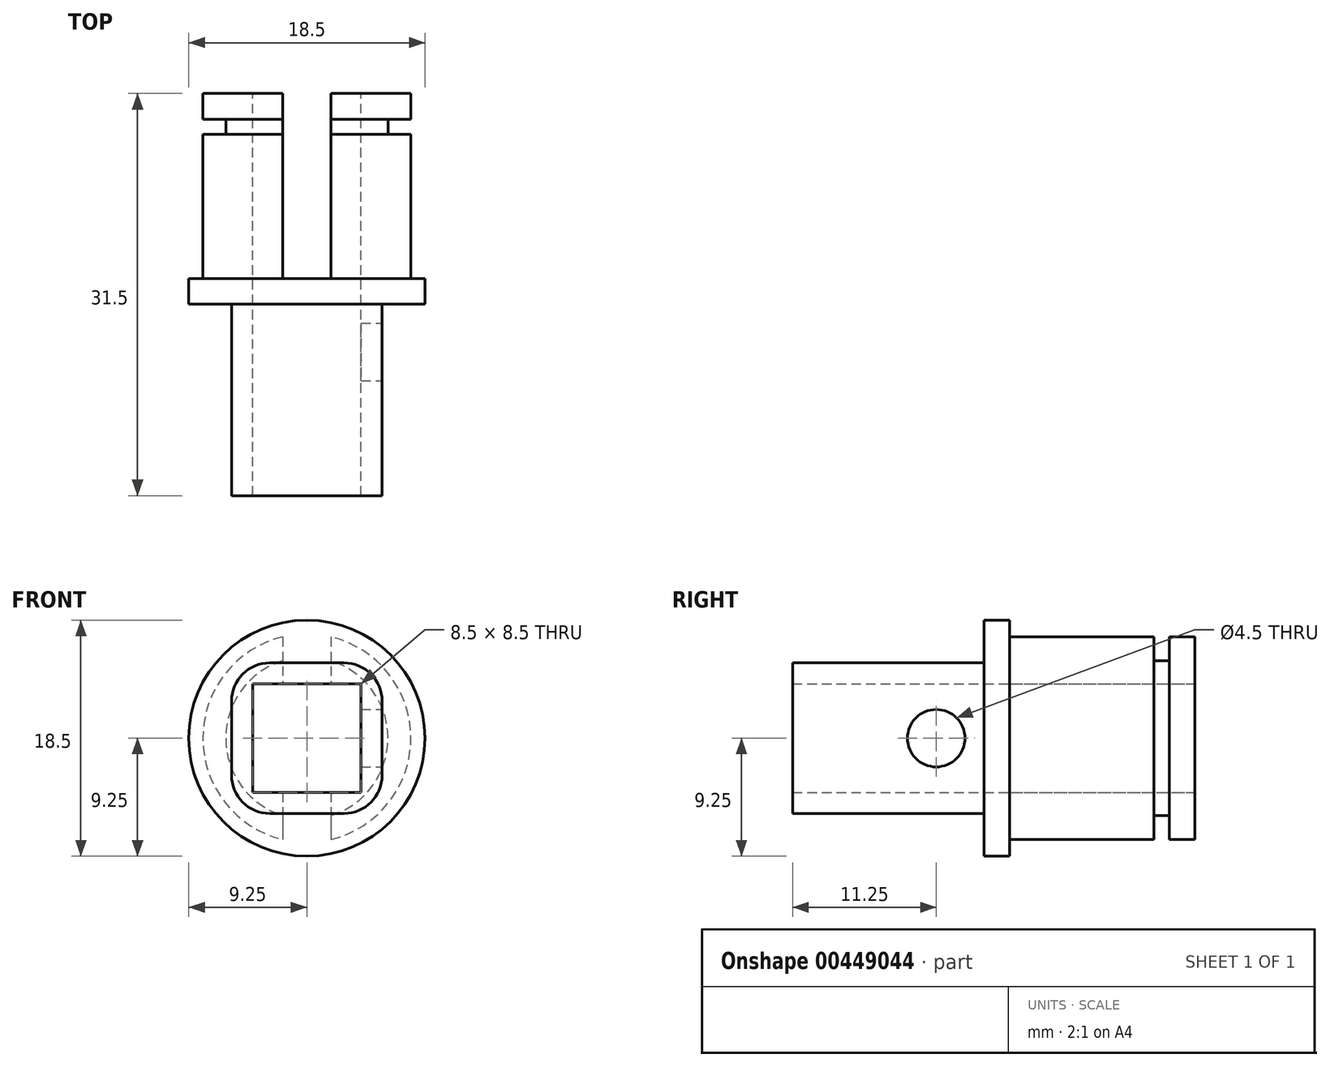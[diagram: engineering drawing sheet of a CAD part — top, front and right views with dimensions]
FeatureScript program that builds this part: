
annotation { "Feature Type Name" : "Feature", "Feature Type Description" : "" }
export const myFeature = defineFeature(function(context is Context, id is Id, definition is map)
    precondition{}
    {
        {
            var Q0;
            Q0=qCreatedBy(makeId("Front.planeOp"),FACE);
            var sketch = newSketch(context, id + "F0", { "sketchPlane" : qUnion([Q0])});
            skCircle(sketch, "E0", {"center": v(0, 0) * mm, "radius": 8.15 * mm});
            skLineSegment(sketch, "E1.bottom", {"start": v(1.9, 7.93) * mm, "end": v(-1.9, 7.93) * mm});
            skLineSegment(sketch, "E1.top", {"start": v(1.9, -7.93) * mm, "end": v(-1.9, -7.93) * mm});
            skLineSegment(sketch, "E1.left", {"start": v(1.9, 7.93) * mm, "end": v(1.9, -7.93) * mm});
            skLineSegment(sketch, "E1.right", {"start": v(-1.9, 7.93) * mm, "end": v(-1.9, -7.93) * mm});
            skLineSegment(sketch, "E2.bottom", {"start": v(-4.25, 4.25) * mm, "end": v(4.25, 4.25) * mm});
            skLineSegment(sketch, "E2.top", {"start": v(-4.25, -4.25) * mm, "end": v(4.25, -4.25) * mm});
            skLineSegment(sketch, "E2.left", {"start": v(-4.25, 4.25) * mm, "end": v(-4.25, -4.25) * mm});
            skLineSegment(sketch, "E2.right", {"start": v(4.25, 4.25) * mm, "end": v(4.25, -4.25) * mm});
            skSolve(sketch);
        }
        {
            var Q0;
            {var subQ0=sQuery(id+"F0.wireOp",EDGE,"E2.right");Q0=makeQuery(id+"F0.imprint","IMPRINT",FACE,{"disambiguationData":[TD([[makeQuery(id+"F0.imprint","IMPRINT",EDGE,{"derivedFrom":subQ0}),1.0]])]});}
            var Q1;
            {var subQ0=sQuery(id+"F0.wireOp",EDGE,"E2.left");Q1=makeQuery(id+"F0.imprint","IMPRINT",FACE,{"disambiguationData":[TD([[makeQuery(id+"F0.imprint","IMPRINT",EDGE,{"derivedFrom":subQ0}),-1.0]])]});}
            extrude(context, id + "F1", {"entities" : qUnion([Q0, Q1]), "depth" : 14.5 * mm});
        }
        {
            var Q0;
            Q0=qCreatedBy(makeId("Right.planeOp"),FACE);
            var sketch = newSketch(context, id + "F2", { "sketchPlane" : qUnion([Q0])});
            skLineSegment(sketch, "E3", {"start": v(0, 0) * mm, "end": v(-2, 0) * mm, "construction": true});
            skLineSegment(sketch, "E4", {"start": v(-25, 8.15) * mm, "end": v(0, 8.15) * mm, "construction": true});
            skLineSegment(sketch, "E5", {"start": v(0, 8.15) * mm, "end": v(-2, 8.15) * mm});
            skLineSegment(sketch, "E6", {"start": v(-2, 8.15) * mm, "end": v(-3.2, 8.15) * mm});
            skLineSegment(sketch, "E7", {"start": v(-3.2, 8.15) * mm, "end": v(-3.2, 6.35) * mm});
            skLineSegment(sketch, "E8", {"start": v(-3.2, 6.35) * mm, "end": v(-2, 6.35) * mm});
            skLineSegment(sketch, "E9", {"start": v(-2, 6.35) * mm, "end": v(-2, 8.15) * mm});
            skSolve(sketch);
        }
        {
            var Q0;
            Q0 = qSketchRegion(id + "F2", true);
            var Q1;
            Q1=sQuery(id+"F2.wireOp",EDGE,"E3");
            revolve(context, id + "F3", {"operationType" : NewBodyOperationType.REMOVE, "entities" : qUnion([Q0]), "axis" : qUnion([Q1]), "revolveType" : RevolveType.FULL, "oppositeDirection" : true});
        }
        {
            var Q0;
            Q0=makeQuery(id+"F1.opExtrude","CAP_FACE",FACE,{"disambiguationData":[OSD([sQuery(id+"F0.wireOp",EDGE,"E0"),sQuery(id+"F0.wireOp",EDGE,"E1.left"),sQuery(id+"F0.wireOp",EDGE,"E2.bottom"),sQuery(id+"F0.wireOp",EDGE,"E2.top"),sQuery(id+"F0.wireOp",EDGE,"E2.right")])],"isStart":false});
            var sketch = newSketch(context, id + "F4", { "sketchPlane" : qUnion([Q0])});
            skCircle(sketch, "E10", {"center": v(0, 0) * mm, "radius": 9.25 * mm});
            skSolve(sketch);
        }
        {
            var Q0;
            Q0 = qSketchRegion(id + "F4", true);
            extrude(context, id + "F5", {"entities" : qUnion([Q0]), "operationType" : NewBodyOperationType.ADD, "depth" : 2 * mm});
        }
        {
            var Q0;
            Q0=makeQuery(id+"F5.opExtrude","CAP_FACE",FACE,{"disambiguationData":[OSD([sQuery(id+"F4.wireOp",EDGE,"E10")])],"isStart":false});
            var sketch = newSketch(context, id + "F6", { "sketchPlane" : qUnion([Q0])});
            skLineSegment(sketch, "E11.0", {"start": v(-4.25, 4.25) * mm, "end": v(-4.25, -4.25) * mm});
            skLineSegment(sketch, "E12.0", {"start": v(-4.25, 4.25) * mm, "end": v(4.25, 4.25) * mm});
            skLineSegment(sketch, "E13.0", {"start": v(4.25, 4.25) * mm, "end": v(4.25, -4.25) * mm});
            skLineSegment(sketch, "E14.0", {"start": v(-4.25, -4.25) * mm, "end": v(4.25, -4.25) * mm});
            skLineSegment(sketch, "E15.bottom", {"start": v(5.9, 5.9) * mm, "end": v(-5.9, 5.9) * mm});
            skLineSegment(sketch, "E15.top", {"start": v(5.9, -5.9) * mm, "end": v(-5.9, -5.9) * mm});
            skLineSegment(sketch, "E15.left", {"start": v(5.9, 5.9) * mm, "end": v(5.9, -5.9) * mm});
            skLineSegment(sketch, "E15.right", {"start": v(-5.9, 5.9) * mm, "end": v(-5.9, -5.9) * mm});
            skPoint(sketch, "E15.middle", {"position": v(0, 0) * mm});
            skSolve(sketch);
        }
        {
            var Q0;
            Q0=makeQuery(id+"F6.imprint","IMPRINT",FACE,{"disambiguationData":[TD([[makeQuery(id+"F6.imprint","IMPRINT",EDGE,{"derivedFrom":sQuery(id+"F6.wireOp",EDGE,"E11.0")}),-1.0]])]});
            extrude(context, id + "F7", {"entities" : qUnion([Q0]), "depth" : 15 * mm});
        }
        {
            var Q0;
            Q0=makeQuery(id+"F7.opExtrude","SWEPT_FACE",FACE,{"disambiguationData":[OSD([sQuery(id+"F6.wireOp",EDGE,"E15.left")])]});
            var sketch = newSketch(context, id + "F8", { "sketchPlane" : qUnion([Q0])});
            skLineSegment(sketch, "E16", {"start": v(-16.5, 0) * mm, "end": v(-18, 0) * mm});
            skPoint(sketch, "E16.endSnap0", {"position": v(-16.5, 0) * mm});
            skCircle(sketch, "E17", {"center": v(-20.25, 0) * mm, "radius": 2.25 * mm});
            skSolve(sketch);
        }
        {
            var Q0;
            Q0=makeQuery(id+"F8.imprint","IMPRINT",FACE,{"disambiguationData":[TD([[makeQuery(id+"F8.imprint","IMPRINT",EDGE,{"derivedFrom":sQuery(id+"F8.wireOp",EDGE,"E17")}),1.0]])]});
            extrude(context, id + "F9", {"entities" : qUnion([Q0]), "operationType" : NewBodyOperationType.REMOVE, "endBound" : BoundingType.UP_TO_NEXT, "oppositeDirection" : true, "depth" : 25 * mm});
        }
        {
            var Q0;
            Q0=makeQuery(id+"F7.opExtrude","SWEPT_EDGE",EDGE,{"disambiguationData":[OSD([sQuery(id+"F6.wireOp",EDGE,"E15.bottom"),sQuery(id+"F6.wireOp",EDGE,"E15.right")])]});
            var Q1;
            Q1=makeQuery(id+"F7.opExtrude","SWEPT_EDGE",EDGE,{"disambiguationData":[OSD([sQuery(id+"F6.wireOp",EDGE,"E15.top"),sQuery(id+"F6.wireOp",EDGE,"E15.right")])]});
            var Q2;
            Q2=makeQuery(id+"F7.opExtrude","SWEPT_EDGE",EDGE,{"disambiguationData":[OSD([sQuery(id+"F6.wireOp",EDGE,"E15.bottom"),sQuery(id+"F6.wireOp",EDGE,"E15.left")])]});
            var Q3;
            Q3=makeQuery(id+"F7.opExtrude","SWEPT_EDGE",EDGE,{"disambiguationData":[OSD([sQuery(id+"F6.wireOp",EDGE,"E15.top"),sQuery(id+"F6.wireOp",EDGE,"E15.left")])]});
            fillet(context, id + "F10", {"entities" : qUnion([Q0, Q1, Q2, Q3]), "radius" : 3 * mm, "tangentPropagation" : true, "allowEdgeOverflow" : false});
        }
        {
            var Q0;
            Q0=makeQuery(id+"F6.imprint","IMPRINT",FACE,{"disambiguationData":[TD([[makeQuery(id+"F6.imprint","IMPRINT",EDGE,{"derivedFrom":sQuery(id+"F6.wireOp",EDGE,"E11.0")}),1.0]])]});
            extrude(context, id + "F11", {"entities" : qUnion([Q0]), "operationType" : NewBodyOperationType.REMOVE, "endBound" : BoundingType.THROUGH_ALL, "oppositeDirection" : true, "depth" : 25 * mm});
        }
    });
